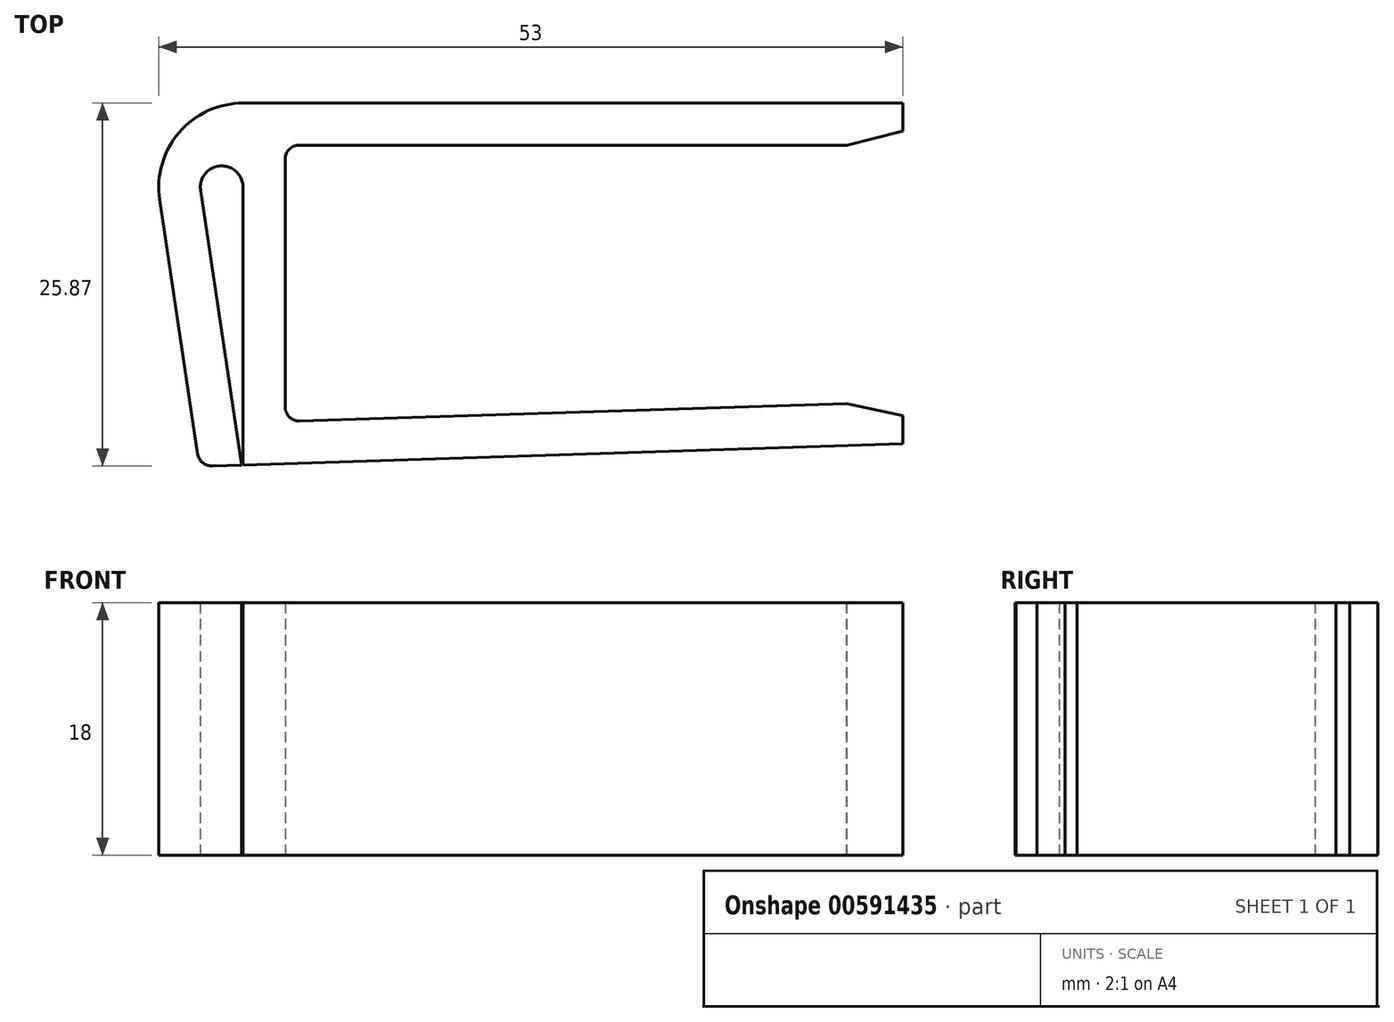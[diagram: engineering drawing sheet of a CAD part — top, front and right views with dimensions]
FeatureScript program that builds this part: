
annotation { "Feature Type Name" : "Feature", "Feature Type Description" : "" }
export const myFeature = defineFeature(function(context is Context, id is Id, definition is map)
    precondition{}
    {
        {
            var Q0;
            Q0=qCreatedBy(makeId("Top.planeOp"),FACE);
            var sketch = newSketch(context, id + "F0", { "sketchPlane" : qUnion([Q0])});
            skLineSegment(sketch, "E0", {"start": v(44, 0) * mm, "end": v(0, 0) * mm});
            skLineSegment(sketch, "E1", {"start": v(0, 0) * mm, "end": v(0, -19.7) * mm});
            skLineSegment(sketch, "E2", {"start": v(0, -19.7) * mm, "end": v(44, -18.3) * mm});
            skLineSegment(sketch, "E3", {"start": v(44, 0) * mm, "end": v(44, 3) * mm});
            skLineSegment(sketch, "E4", {"start": v(44, 3) * mm, "end": v(-3, 3) * mm});
            skLineSegment(sketch, "E5", {"start": v(-3, 3) * mm, "end": v(-3, -22.8) * mm});
            skLineSegment(sketch, "E6", {"start": v(-3, -22.8) * mm, "end": v(44, -21.3) * mm});
            skLineSegment(sketch, "E7", {"start": v(44, -21.3) * mm, "end": v(44, -18.3) * mm});
            skSolve(sketch);
        }
        {
            var Q0;
            Q0=qSketchRegion(id+"F0",true);
            extrude(context, id + "F1", {"entities" : qUnion([Q0]), "depth" : 9 * mm, "offsetDistance" : 25 * mm, "hasSecondDirection" : true, "secondDirectionOppositeDirection" : true, "secondDirectionDepth" : 9 * mm});
        }
        {
            var Q0;
            Q0=qCreatedBy(makeId("Top.planeOp"),FACE);
            var sketch = newSketch(context, id + "F2", { "sketchPlane" : qUnion([Q0])});
            skLineSegment(sketch, "E8", {"start": v(-8.94, -3.9) * mm, "end": v(-6.1, -22.9) * mm});
            skLineSegment(sketch, "E9", {"start": v(-6.1, -22.9) * mm, "end": v(-3.1, -22.8) * mm});
            skLineSegment(sketch, "E10", {"start": v(-3.1, -22.8) * mm, "end": v(-6.03, -3.22) * mm});
            skArc(sketch, "E11", {"start": v(-3, -3) * mm, "mid": v(-4.63, -1.48) * mm, "end": v(-6.03, -3.22) * mm});
            skPoint(sketch, "E12.orphan", {"position": v(-3.1, 12.76) * mm});
            skLineSegment(sketch, "E13", {"start": v(-3, 3) * mm, "end": v(-3, -3) * mm});
            skArc(sketch, "E14", {"start": v(-3, 3) * mm, "mid": v(-7.55, 0.92) * mm, "end": v(-8.94, -3.9) * mm});
            skSolve(sketch);
        }
        {
            var Q0;
            Q0=qSketchRegion(id+"F2",true);
            extrude(context, id + "F3", {"entities" : qUnion([Q0]), "operationType" : NewBodyOperationType.ADD, "depth" : 9 * mm, "offsetDistance" : 25 * mm, "hasSecondDirection" : true, "secondDirectionOppositeDirection" : true, "secondDirectionDepth" : 9 * mm});
        }
        {
            var Q0;
            Q0=makeQuery(id+"F3.opExtrude","SWEPT_EDGE",EDGE,{"disambiguationData":[OSD([sQuery(id+"F2.wireOp",EDGE,"Lq6Fhy1j-hPK5-R32y-x797-HyNdTWa8Dpb7"),sQuery(id+"F2.wireOp",EDGE,"PX8Bem3X-2fIm-P0Cq-m5Nu-ZZc5qn9Ji6NO")])]});
            var Q1;
            Q1=makeQuery(id+"F3.opExtrude","SWEPT_EDGE",EDGE,{"disambiguationData":[OSD([sQuery(id+"F2.wireOp",EDGE,"LXNDoJ7h-ih2n-xskl-bUCd-Vp6MB182eyXe"),sQuery(id+"F2.wireOp",EDGE,"Lq6Fhy1j-hPK5-R32y-x797-HyNdTWa8Dpb7")])]});
            var Q2;
            Q2=makeQuery(id+"F3.boolean.opBoolean","MERGE",EDGE,{"derivedFrom":[makeQuery(id+"F1.opExtrude","SWEPT_EDGE",EDGE,{"disambiguationData":[OSD([sQuery(id+"F0.wireOp",EDGE,"E4"),sQuery(id+"F0.wireOp",EDGE,"E5")])]}),makeQuery(id+"F3.opExtrude","SWEPT_EDGE",EDGE,{"disambiguationData":[OSD([sQuery(id+"F2.wireOp",EDGE,"znsehldE-1eQ1-HR8u-s0M4-TErj0GhLcbnh"),sQuery(id+"F2.wireOp",EDGE,"E13")])]})]});
            var Q3;
            Q3=makeQuery(id+"F3.opExtrude","SWEPT_EDGE",EDGE,{"disambiguationData":[OSD([sQuery(id+"F2.wireOp",EDGE,"E8"),sQuery(id+"F2.wireOp",EDGE,"E9")])]});
            fillet(context, id + "F4", {"entities" : qUnion([Q0, Q1, Q2, Q3]), "radius" : 1 * mm, "tangentPropagation" : true, "allowEdgeOverflow" : false});
        }
        {
            var Q0;
            Q0=makeQuery(id+"F1.opExtrude","SWEPT_EDGE",EDGE,{"disambiguationData":[OSD([sQuery(id+"F0.wireOp",EDGE,"E0"),sQuery(id+"F0.wireOp",EDGE,"E1")])]});
            var Q1;
            Q1=makeQuery(id+"F1.opExtrude","SWEPT_EDGE",EDGE,{"disambiguationData":[OSD([sQuery(id+"F0.wireOp",EDGE,"E1"),sQuery(id+"F0.wireOp",EDGE,"E2")])]});
            fillet(context, id + "F5", {"entities" : qUnion([Q0, Q1]), "radius" : 1 * mm, "tangentPropagation" : true, "allowEdgeOverflow" : false});
        }
        {
            var Q0;
            Q0=makeQuery(id+"F1.opExtrude","SWEPT_EDGE",EDGE,{"disambiguationData":[OSD([sQuery(id+"F0.wireOp",EDGE,"E0"),sQuery(id+"F0.wireOp",EDGE,"E3")])]});
            chamfer(context, id + "F6", {"entities" : qUnion([Q0]), "chamferType" : ChamferType.TWO_OFFSETS, "width1" : 1 * mm, "oppositeDirection" : false, "width2" : 4 * mm, "tangentPropagation" : true});
        }
        {
            var Q0;
            Q0=makeQuery(id+"F1.opExtrude","SWEPT_EDGE",EDGE,{"disambiguationData":[OSD([sQuery(id+"F0.wireOp",EDGE,"E2"),sQuery(id+"F0.wireOp",EDGE,"E7")])]});
            chamfer(context, id + "F7", {"entities" : qUnion([Q0]), "chamferType" : ChamferType.TWO_OFFSETS, "width1" : 1 * mm, "oppositeDirection" : true, "width2" : 4 * mm, "tangentPropagation" : true});
        }
    });
